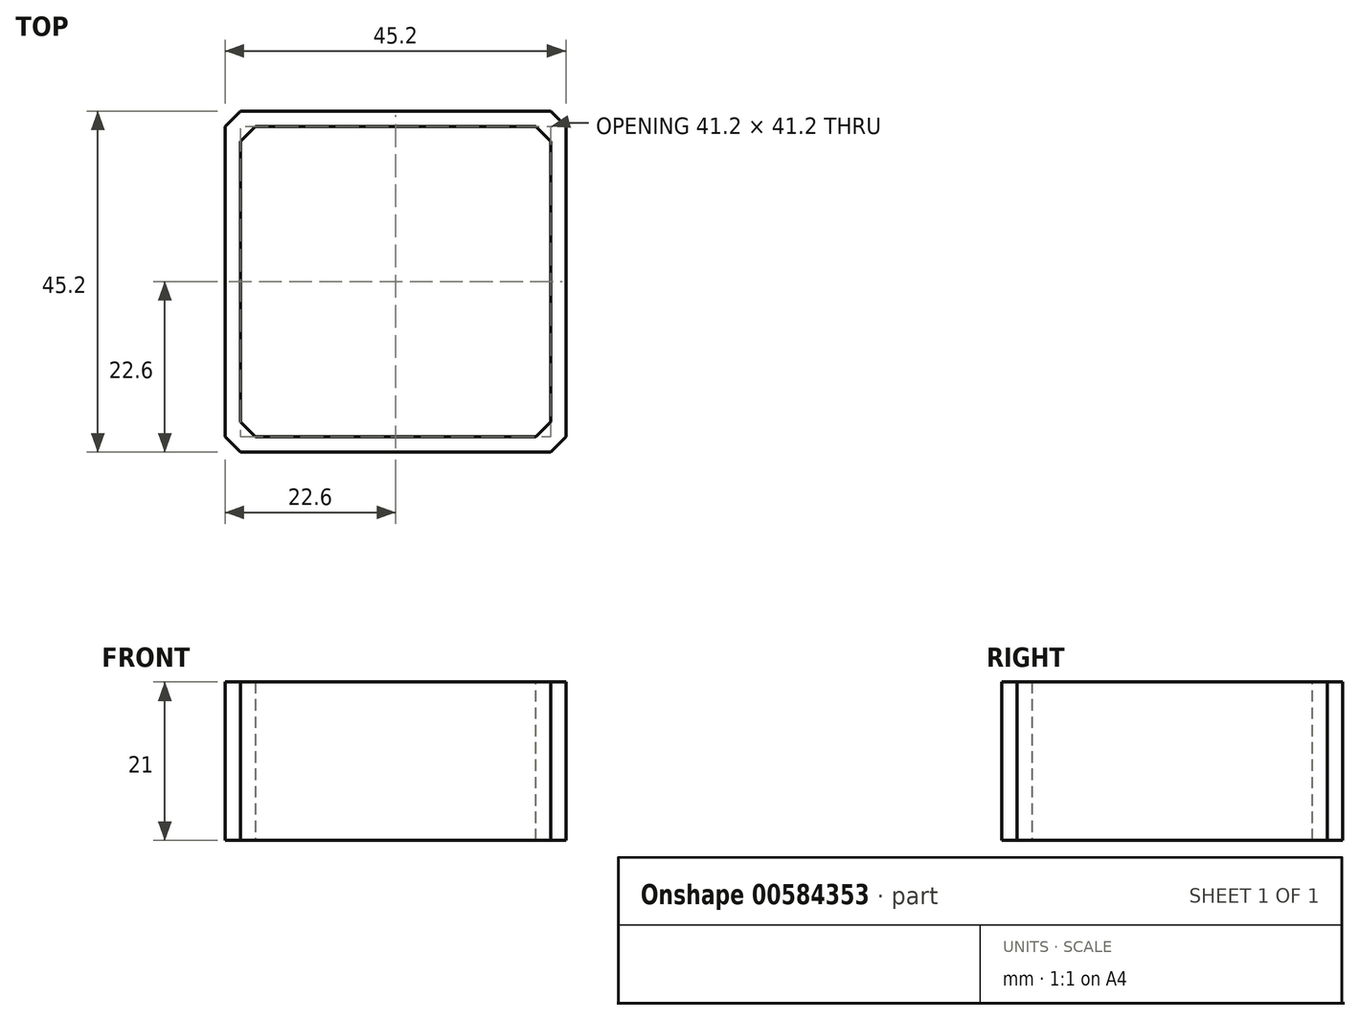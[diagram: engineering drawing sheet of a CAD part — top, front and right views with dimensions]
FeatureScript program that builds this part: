
annotation { "Feature Type Name" : "Feature", "Feature Type Description" : "" }
export const myFeature = defineFeature(function(context is Context, id is Id, definition is map)
    precondition{}
    {
        {
            var Q0;
            Q0=qCreatedBy(makeId("Top.planeOp"),FACE);
            var sketch = newSketch(context, id + "F0", { "sketchPlane" : qUnion([Q0])});
            skLineSegment(sketch, "E0.bottom", {"start": v(-22.6, 22.6) * mm, "end": v(22.6, 22.6) * mm});
            skLineSegment(sketch, "E0.top", {"start": v(-22.6, -22.6) * mm, "end": v(22.6, -22.6) * mm});
            skLineSegment(sketch, "E0.left", {"start": v(-22.6, 22.6) * mm, "end": v(-22.6, -22.6) * mm});
            skLineSegment(sketch, "E0.right", {"start": v(22.6, 22.6) * mm, "end": v(22.6, -22.6) * mm});
            skPoint(sketch, "E0.middle", {"position": v(0, 0) * mm});
            skLineSegment(sketch, "E1.0", {"start": v(-20.6, 20.6) * mm, "end": v(20.6, 20.6) * mm});
            skLineSegment(sketch, "E1.1", {"start": v(-20.6, 20.6) * mm, "end": v(-20.6, -20.6) * mm});
            skLineSegment(sketch, "E1.2", {"start": v(-20.6, -20.6) * mm, "end": v(20.6, -20.6) * mm});
            skLineSegment(sketch, "E1.3", {"start": v(20.6, 20.6) * mm, "end": v(20.6, -20.6) * mm});
            skSolve(sketch);
        }
        {
            var Q0;
            Q0=makeQuery(id+"F0.imprint","IMPRINT",FACE,{"disambiguationData":[TD([[makeQuery(id+"F0.imprint","IMPRINT",EDGE,{"derivedFrom":sQuery(id+"F0.wireOp",EDGE,"E0.bottom")}),-1.0]])]});
            extrude(context, id + "F1", {"entities" : qUnion([Q0]), "depth" : 21 * mm, "offsetDistance" : 25 * mm});
        }
        {
            var Q0;
            Q0=makeQuery(id+"F1.opExtrude","SWEPT_EDGE",EDGE,{"disambiguationData":[OSD([sQuery(id+"F0.wireOp",EDGE,"E0.top"),sQuery(id+"F0.wireOp",EDGE,"E0.left")])]});
            var Q1;
            Q1=makeQuery(id+"F1.opExtrude","SWEPT_EDGE",EDGE,{"disambiguationData":[OSD([sQuery(id+"F0.wireOp",EDGE,"E1.1"),sQuery(id+"F0.wireOp",EDGE,"E1.2")])]});
            var Q2;
            Q2=makeQuery(id+"F1.opExtrude","SWEPT_EDGE",EDGE,{"disambiguationData":[OSD([sQuery(id+"F0.wireOp",EDGE,"E0.top"),sQuery(id+"F0.wireOp",EDGE,"E0.right")])]});
            var Q3;
            Q3=makeQuery(id+"F1.opExtrude","SWEPT_EDGE",EDGE,{"disambiguationData":[OSD([sQuery(id+"F0.wireOp",EDGE,"E1.2"),sQuery(id+"F0.wireOp",EDGE,"E1.3")])]});
            var Q4;
            Q4=makeQuery(id+"F1.opExtrude","SWEPT_EDGE",EDGE,{"disambiguationData":[OSD([sQuery(id+"F0.wireOp",EDGE,"E1.0"),sQuery(id+"F0.wireOp",EDGE,"E1.3")])]});
            var Q5;
            Q5=makeQuery(id+"F1.opExtrude","SWEPT_EDGE",EDGE,{"disambiguationData":[OSD([sQuery(id+"F0.wireOp",EDGE,"E1.0"),sQuery(id+"F0.wireOp",EDGE,"E1.1")])]});
            var Q6;
            Q6=makeQuery(id+"F1.opExtrude","SWEPT_EDGE",EDGE,{"disambiguationData":[OSD([sQuery(id+"F0.wireOp",EDGE,"E0.bottom"),sQuery(id+"F0.wireOp",EDGE,"E0.right")])]});
            var Q7;
            Q7=makeQuery(id+"F1.opExtrude","SWEPT_EDGE",EDGE,{"disambiguationData":[OSD([sQuery(id+"F0.wireOp",EDGE,"E0.bottom"),sQuery(id+"F0.wireOp",EDGE,"E0.left")])]});
            chamfer(context, id + "F2", {"entities" : qUnion([Q0, Q1, Q2, Q3, Q4, Q5, Q6, Q7]), "width" : 2 * mm, "tangentPropagation" : true});
        }
    });
